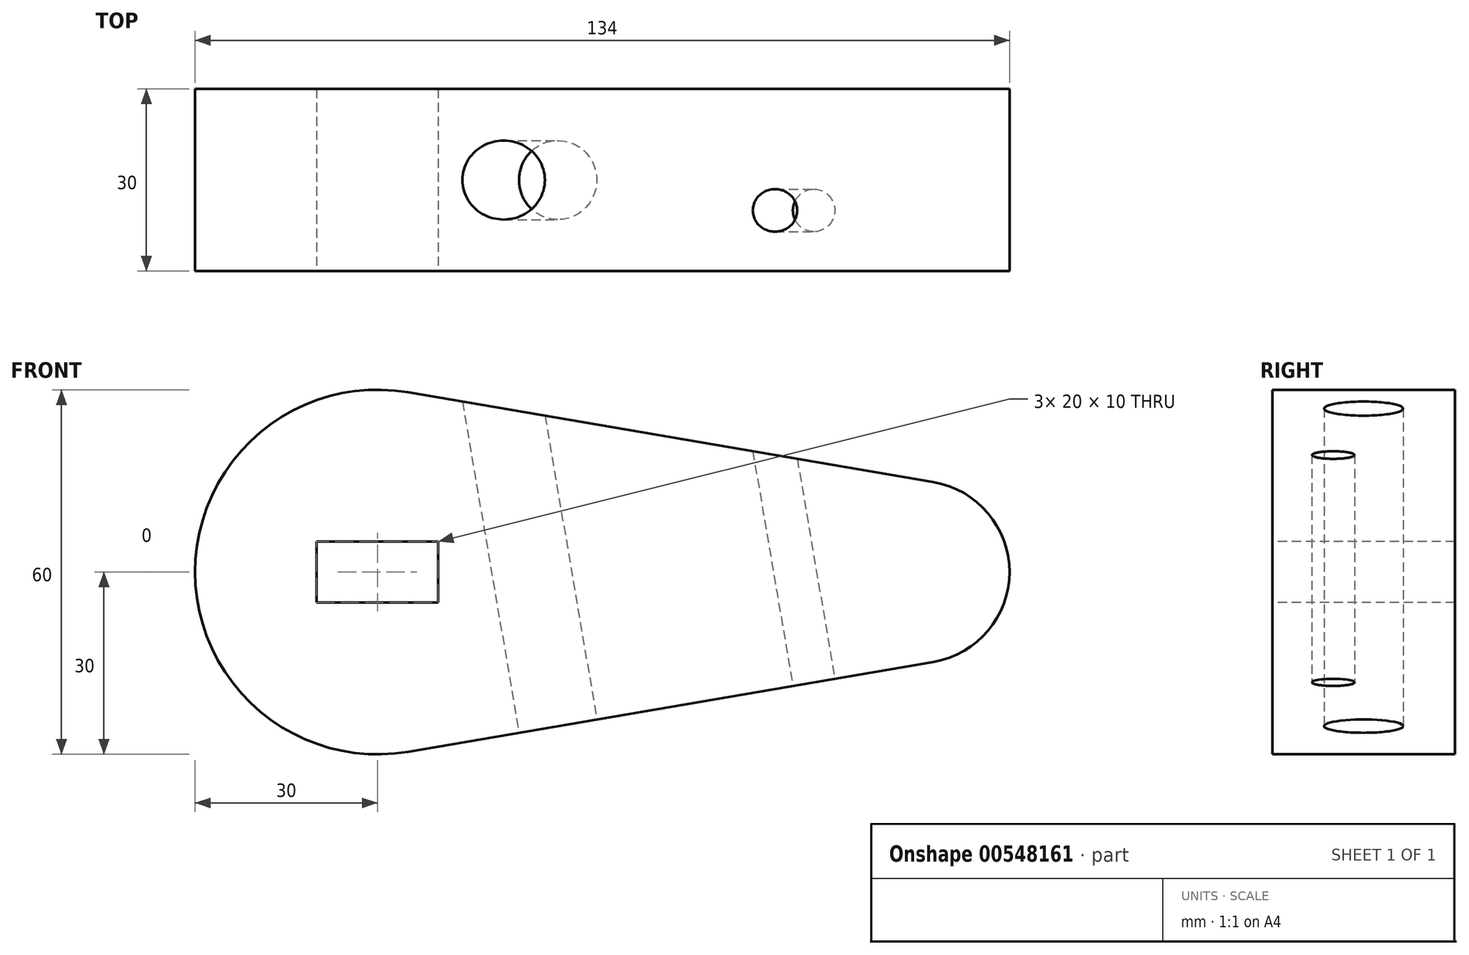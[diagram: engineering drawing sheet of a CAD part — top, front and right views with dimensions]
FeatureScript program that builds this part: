
annotation { "Feature Type Name" : "Feature", "Feature Type Description" : "" }
export const myFeature = defineFeature(function(context is Context, id is Id, definition is map)
    precondition{}
    {
        {
            var Q0;
            Q0=qCreatedBy(makeId("Front.planeOp"),FACE);
            var sketch = newSketch(context, id + "F0", { "sketchPlane" : qUnion([Q0])});
            skArc(sketch, "E0", {"start": v(5.06, 29.57) * mm, "mid": v(-30, 0) * mm, "end": v(5.06, -29.57) * mm});
            skArc(sketch, "E1", {"start": v(91.53, -14.79) * mm, "mid": v(104, 0) * mm, "end": v(91.53, 14.79) * mm});
            skLineSegment(sketch, "E2", {"start": v(5.06, 29.57) * mm, "end": v(91.53, 14.79) * mm});
            skLineSegment(sketch, "E3", {"start": v(5.06, -29.57) * mm, "end": v(91.53, -14.79) * mm});
            skSolve(sketch);
        }
        {
            var Q0;
            Q0=makeQuery(id+"F0.imprint","IMPRINT",FACE,{"disambiguationData":[TD([[makeQuery(id+"F0.imprint","IMPRINT",EDGE,{"derivedFrom":sQuery(id+"F0.wireOp",EDGE,"E0")}),1.0]])]});
            extrude(context, id + "F1", {"entities" : qUnion([Q0]), "depth" : 30 * mm, "offsetDistance" : 25 * mm});
        }
        {
            var Q0;
            Q0=makeQuery(id+"F1.opExtrude","CAP_FACE",FACE,{"disambiguationData":[OSD([sQuery(id+"F0.wireOp",EDGE,"E0"),sQuery(id+"F0.wireOp",EDGE,"E1"),sQuery(id+"F0.wireOp",EDGE,"E2"),sQuery(id+"F0.wireOp",EDGE,"E3")])],"isStart":false});
            var sketch = newSketch(context, id + "F2", { "sketchPlane" : qUnion([Q0])});
            skLineSegment(sketch, "E4.bottom", {"start": v(10, -5) * mm, "end": v(-10, -5) * mm});
            skLineSegment(sketch, "E4.top", {"start": v(10, 5) * mm, "end": v(-10, 5) * mm});
            skLineSegment(sketch, "E4.left", {"start": v(10, -5) * mm, "end": v(10, 5) * mm});
            skLineSegment(sketch, "E4.right", {"start": v(-10, -5) * mm, "end": v(-10, 5) * mm});
            skPoint(sketch, "E4.middle", {"position": v(0, 0) * mm});
            skSolve(sketch);
        }
        {
            var Q0;
            Q0=makeQuery(id+"F2.imprint","IMPRINT",FACE,{"disambiguationData":[TD([[makeQuery(id+"F2.imprint","IMPRINT",EDGE,{"derivedFrom":sQuery(id+"F2.wireOp",EDGE,"E4.bottom")}),-1.0]])]});
            extrude(context, id + "F3", {"entities" : qUnion([Q0]), "operationType" : NewBodyOperationType.REMOVE, "oppositeDirection" : true, "depth" : 30 * mm, "offsetDistance" : 25 * mm});
        }
        {
            var Q0;
            Q0=makeQuery(id+"F1.opExtrude","SWEPT_FACE",FACE,{"disambiguationData":[OSD([sQuery(id+"F0.wireOp",EDGE,"E3")])]});
            var sketch = newSketch(context, id + "F4", { "sketchPlane" : qUnion([Q0])});
            skCircle(sketch, "E5", {"center": v(25, 15) * mm, "radius": 6.5 * mm});
            skSolve(sketch);
        }
        {
            var Q0;
            Q0=makeQuery(id+"F4.imprint","IMPRINT",FACE,{"disambiguationData":[TD([[makeQuery(id+"F4.imprint","IMPRINT",EDGE,{"derivedFrom":sQuery(id+"F4.wireOp",EDGE,"E5")}),1.0]])]});
            extrude(context, id + "F5", {"entities" : qUnion([Q0]), "operationType" : NewBodyOperationType.REMOVE, "endBound" : BoundingType.THROUGH_ALL, "oppositeDirection" : true, "depth" : 25 * mm, "offsetDistance" : 25 * mm});
        }
        {
            var Q0;
            Q0=makeQuery(id+"F1.opExtrude","SWEPT_FACE",FACE,{"disambiguationData":[OSD([sQuery(id+"F0.wireOp",EDGE,"E3")])]});
            var sketch = newSketch(context, id + "F6", { "sketchPlane" : qUnion([Q0])});
            skPoint(sketch, "E6", {"position": v(67.73, 20) * mm});
            skSolve(sketch);
        }
        {
            var Q0;
            Q0=sQuery(id+"F6.wireOp",VERTEX,"E6");
            var Q1;
            Q1=makeQuery(id+"F1.opExtrude","SWEPT_BODY",BODY,{"disambiguationData":[OSD([sQuery(id+"F0.wireOp",EDGE,"E0"),sQuery(id+"F0.wireOp",EDGE,"E1"),sQuery(id+"F0.wireOp",EDGE,"E2"),sQuery(id+"F0.wireOp",EDGE,"E3")])]});
            hole(context, id + "F7", {"style" : HoleStyle.SIMPLE, "endStyle" : HoleEndStyle.THROUGH, "holeDiameter" : 7 * mm, "isTappedThrough" : true, "tappedDepth" : 12 * mm, "tapClearance" : 3, "locations" : qUnion([Q0]), "scope" : qUnion([Q1])});
        }
    });
